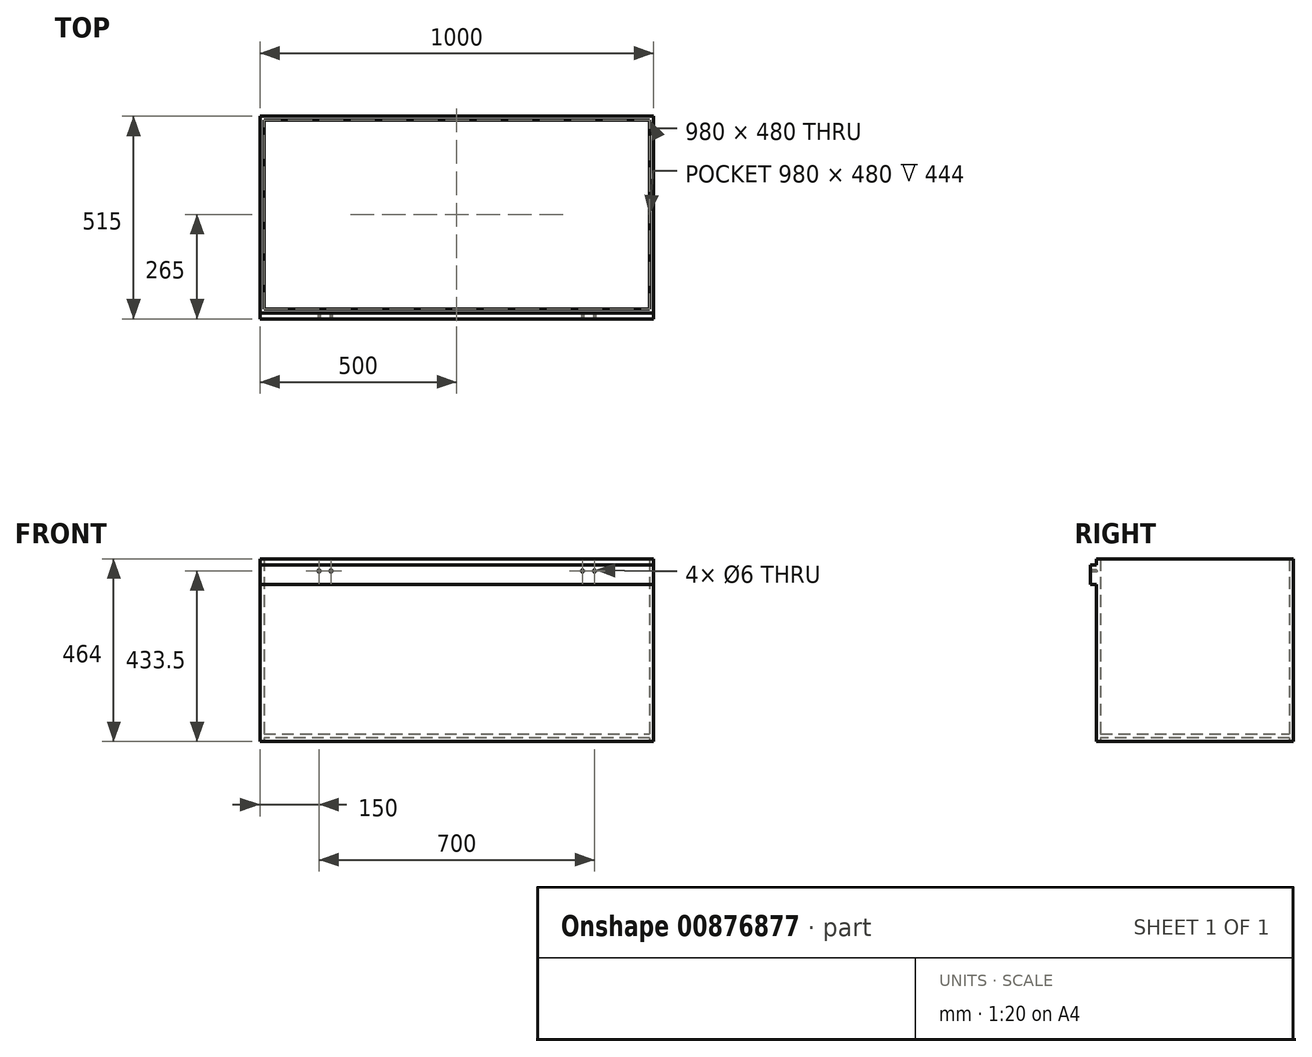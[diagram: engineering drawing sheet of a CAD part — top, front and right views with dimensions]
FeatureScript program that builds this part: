
annotation { "Feature Type Name" : "Feature", "Feature Type Description" : "" }
export const myFeature = defineFeature(function(context is Context, id is Id, definition is map)
    precondition{}
    {
        {
            var Q0;
            Q0=qCreatedBy(makeId("Top.planeOp"),FACE);
            var sketch = newSketch(context, id + "F0", { "sketchPlane" : qUnion([Q0])});
            skLineSegment(sketch, "E0.bottom", {"start": v(500, 250) * mm, "end": v(-500, 250) * mm});
            skLineSegment(sketch, "E0.top", {"start": v(500, -250) * mm, "end": v(-500, -250) * mm});
            skLineSegment(sketch, "E0.left", {"start": v(500, 250) * mm, "end": v(500, -250) * mm});
            skLineSegment(sketch, "E0.right", {"start": v(-500, 250) * mm, "end": v(-500, -250) * mm});
            skPoint(sketch, "E0.middle", {"position": v(0, 0) * mm});
            skSolve(sketch);
        }
        {
            var Q0;
            Q0=makeQuery(id+"F0.imprint","IMPRINT",FACE,{"disambiguationData":[TD([[makeQuery(id+"F0.imprint","IMPRINT",EDGE,{"derivedFrom":sQuery(id+"F0.wireOp",EDGE,"E0.bottom")}),1.0]])]});
            extrude(context, id + "F1", {"entities" : qUnion([Q0]), "depth" : (500 - 36) * mm, "offsetDistance" : 25 * mm});
        }
        {
            var Q0;
            Q0=makeQuery(id+"F1.opExtrude","CAP_FACE",FACE,{"disambiguationData":[OSD([sQuery(id+"F0.wireOp",EDGE,"E0.bottom"),sQuery(id+"F0.wireOp",EDGE,"E0.top"),sQuery(id+"F0.wireOp",EDGE,"E0.left"),sQuery(id+"F0.wireOp",EDGE,"E0.right")])],"isStart":true});
            var sketch = newSketch(context, id + "F2", { "sketchPlane" : qUnion([Q0])});
            skLineSegment(sketch, "E1.0", {"start": v(490, 240) * mm, "end": v(-490, 240) * mm});
            skLineSegment(sketch, "E1.1", {"start": v(490, -240) * mm, "end": v(490, 240) * mm});
            skLineSegment(sketch, "E1.2", {"start": v(-490, -240) * mm, "end": v(490, -240) * mm});
            skLineSegment(sketch, "E1.3", {"start": v(-490, 240) * mm, "end": v(-490, -240) * mm});
            skSolve(sketch);
        }
        {
            var Q0;
            Q0=makeQuery(id+"F2.imprint","IMPRINT",FACE,{"disambiguationData":[TD([[makeQuery(id+"F2.imprint","IMPRINT",EDGE,{"derivedFrom":sQuery(id+"F2.wireOp",EDGE,"E1.0")}),1.0]])]});
            extrude(context, id + "F3", {"entities" : qUnion([Q0]), "operationType" : NewBodyOperationType.REMOVE, "oppositeDirection" : true, "depth" : 10 * mm, "offsetDistance" : 25 * mm});
        }
        {
            var Q0;
            Q0=makeQuery(id+"F1.opExtrude","CAP_FACE",FACE,{"disambiguationData":[OSD([sQuery(id+"F0.wireOp",EDGE,"E0.bottom"),sQuery(id+"F0.wireOp",EDGE,"E0.top"),sQuery(id+"F0.wireOp",EDGE,"E0.left"),sQuery(id+"F0.wireOp",EDGE,"E0.right")])],"isStart":false});
            shell(context, id + "F4", {"entities" : qUnion([Q0]), "thickness" : 10 * mm});
        }
        {
            var Q0;
            Q0=makeQuery(id+"F1.opExtrude","SWEPT_FACE",FACE,{"disambiguationData":[OSD([sQuery(id+"F0.wireOp",EDGE,"E0.top")])]});
            var sketch = newSketch(context, id + "F5", { "sketchPlane" : qUnion([Q0])});
            skLineSegment(sketch, "E2.bottom", {"start": v(-500, 399) * mm, "end": v(500, 399) * mm});
            skLineSegment(sketch, "E2.top", {"start": v(-500, 449) * mm, "end": v(500, 449) * mm});
            skLineSegment(sketch, "E2.left", {"start": v(-500, 399) * mm, "end": v(-500, 449) * mm});
            skLineSegment(sketch, "E2.right", {"start": v(500, 399) * mm, "end": v(500, 449) * mm});
            skSolve(sketch);
        }
        {
            var Q0;
            Q0=makeQuery(id+"F5.imprint","IMPRINT",FACE,{"disambiguationData":[TD([[makeQuery(id+"F5.imprint","IMPRINT",EDGE,{"derivedFrom":sQuery(id+"F5.wireOp",EDGE,"E2.bottom")}),1.0]])]});
            extrude(context, id + "F6", {"entities" : qUnion([Q0]), "operationType" : NewBodyOperationType.ADD, "depth" : 15 * mm, "offsetDistance" : 25 * mm});
        }
        {
            var Q0;
            Q0=makeQuery(id+"F6.opExtrude","CAP_FACE",FACE,{"disambiguationData":[OSD([sQuery(id+"F5.wireOp",EDGE,"E2.bottom"),sQuery(id+"F5.wireOp",EDGE,"E2.top"),sQuery(id+"F5.wireOp",EDGE,"E2.left"),sQuery(id+"F5.wireOp",EDGE,"E2.right")])],"isStart":false});
            var sketch = newSketch(context, id + "F7", { "sketchPlane" : qUnion([Q0])});
            skPoint(sketch, "E3", {"position": v(-350, 433.5) * mm});
            skPoint(sketch, "E4", {"position": v(-319.5, 433.5) * mm});
            skPoint(sketch, "E5", {"position": v(319.5, 433.5) * mm});
            skPoint(sketch, "E6", {"position": v(350, 433.5) * mm});
            skSolve(sketch);
        }
        {
            var Q0;
            Q0=sQuery(id+"F7.wireOp",VERTEX,"E3");
            var Q1;
            Q1=sQuery(id+"F7.wireOp",VERTEX,"E4");
            var Q2;
            Q2=sQuery(id+"F7.wireOp",VERTEX,"E5");
            var Q3;
            Q3=sQuery(id+"F7.wireOp",VERTEX,"E6");
            var Q4;
            Q4=makeQuery(id+"F1.opExtrude","SWEPT_BODY",BODY,{"disambiguationData":[OSD([sQuery(id+"F0.wireOp",EDGE,"E0.bottom"),sQuery(id+"F0.wireOp",EDGE,"E0.top"),sQuery(id+"F0.wireOp",EDGE,"E0.left"),sQuery(id+"F0.wireOp",EDGE,"E0.right")])]});
            hole(context, id + "F8", {"style" : HoleStyle.SIMPLE, "endStyle" : HoleEndStyle.BLIND, "holeDiameter" : 6 * mm, "majorDiameter" : 5 * mm, "holeDepth" : 15 * mm, "isTappedThrough" : true, "tappedDepth" : 12 * mm, "tapClearance" : 3, "locations" : qUnion([Q0, Q1, Q2, Q3]), "scope" : qUnion([Q4])});
        }
    });
